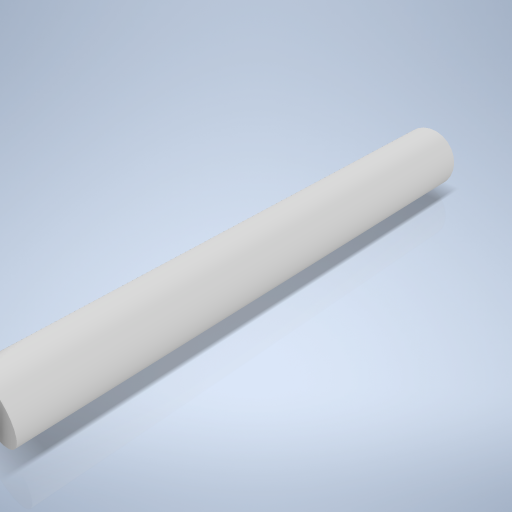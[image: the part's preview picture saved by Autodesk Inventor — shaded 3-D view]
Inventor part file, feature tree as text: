
AUTODESK INVENTOR PART (.ipt)
format: ipt  version: 2024.2 (Build 282272000, 272)  size: 232,960 bytes
history: native  units: mm
features: extrude x1, sketch x1
ambient origin geometry x8: Origin, YZ Plane, XZ Plane, XY Plane, X Axis, Y Axis, Z Axis, Center Point
bodies: Volumenkörper1 (feature_tree)
feature tree (2):
  extrude  "Extrusion1"  Depth=48.0mm TaperAngle=0.0deg
  sketch  "Skizze1"  dims[d0=6.0mm d1=48.0mm d2=0.0mm]
